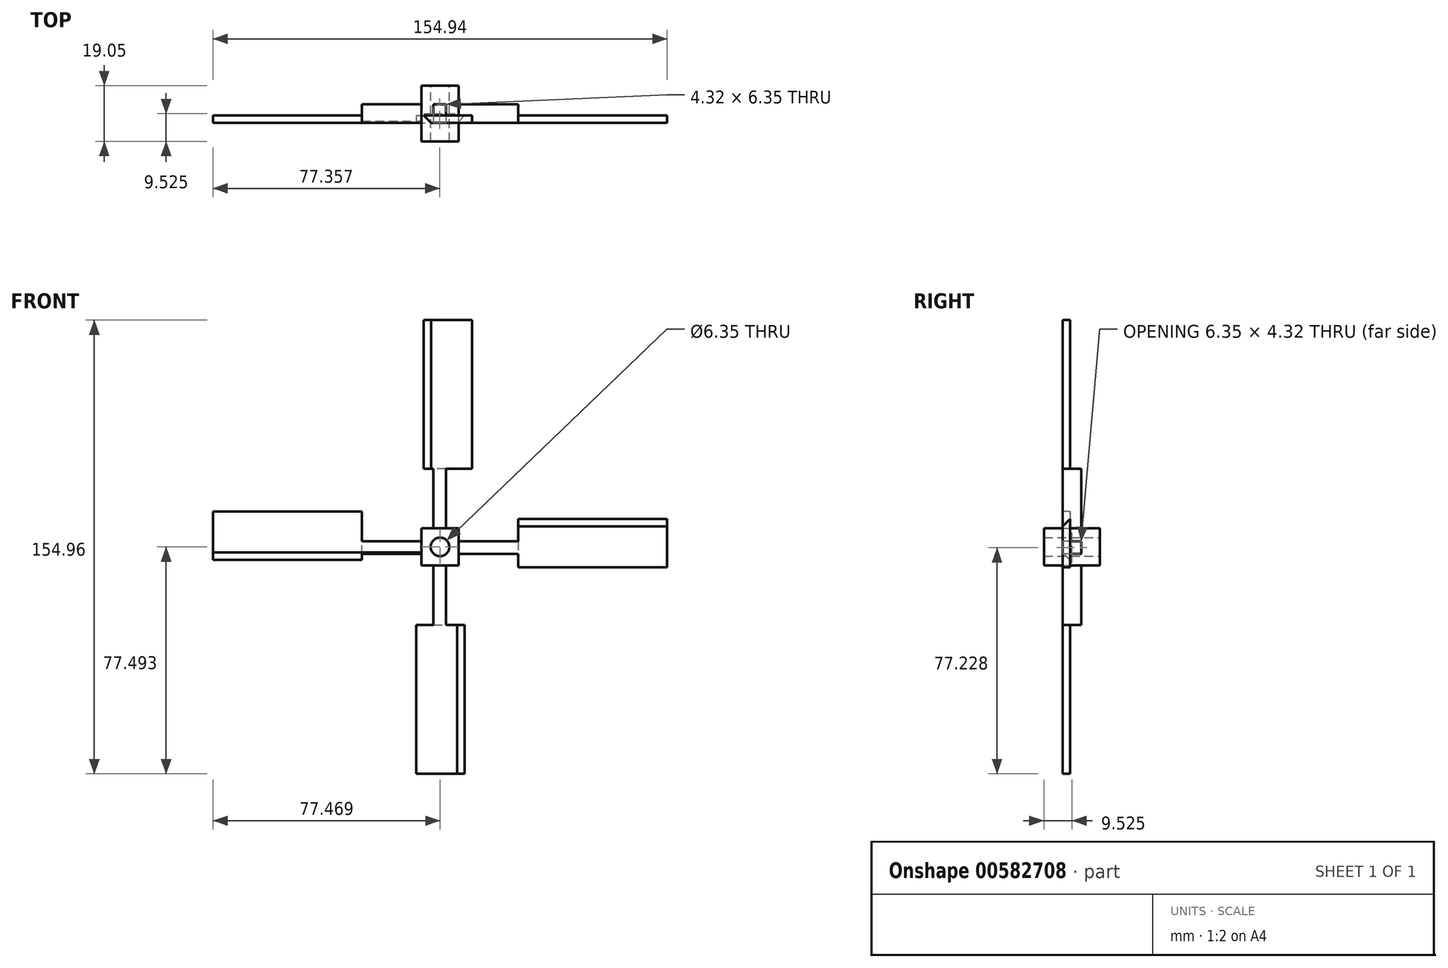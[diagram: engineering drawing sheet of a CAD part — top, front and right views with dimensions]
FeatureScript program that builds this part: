
annotation { "Feature Type Name" : "Feature", "Feature Type Description" : "" }
export const myFeature = defineFeature(function(context is Context, id is Id, definition is map)
    precondition{}
    {
        {
            var Q0;
            Q0=qCreatedBy(makeId("Front.planeOp"),FACE);
            var sketch = newSketch(context, id + "F0", { "sketchPlane" : qUnion([Q0])});
            skLineSegment(sketch, "E0", {"start": v(4.35, 3.5) * mm, "end": v(4.35, -9.2) * mm});
            skLineSegment(sketch, "E1", {"start": v(4.35, -9.2) * mm, "end": v(17.05, -9.2) * mm});
            skLineSegment(sketch, "E2", {"start": v(17.05, -9.2) * mm, "end": v(17.05, 3.5) * mm});
            skLineSegment(sketch, "E3", {"start": v(17.05, 3.5) * mm, "end": v(4.35, 3.5) * mm});
            skCircle(sketch, "E4", {"center": v(10.7, -2.85) * mm, "radius": 3.18 * mm});
            skPoint(sketch, "E4.centerSnap1", {"position": v(4.35, -2.85) * mm});
            skLineSegment(sketch, "E5", {"start": v(17.05, -0.95) * mm, "end": v(37.37, -0.95) * mm});
            skLineSegment(sketch, "E6", {"start": v(37.37, -0.95) * mm, "end": v(37.37, -5.27) * mm});
            skLineSegment(sketch, "E7", {"start": v(37.37, -5.27) * mm, "end": v(17.05, -5.27) * mm});
            skLineSegment(sketch, "E8", {"start": v(4.35, -5.27) * mm, "end": v(-15.97, -5.27) * mm});
            skLineSegment(sketch, "E9", {"start": v(-15.97, -5.27) * mm, "end": v(-15.97, -0.95) * mm});
            skLineSegment(sketch, "E10", {"start": v(-15.97, -0.95) * mm, "end": v(4.35, -0.95) * mm});
            skLineSegment(sketch, "E11", {"start": v(37.37, 9.26) * mm, "end": v(37.37, -0.95) * mm});
            skLineSegment(sketch, "E12", {"start": v(37.37, 9.26) * mm, "end": v(88.17, 9.26) * mm});
            skLineSegment(sketch, "E13", {"start": v(88.17, 9.26) * mm, "end": v(88.17, -9.79) * mm});
            skLineSegment(sketch, "E14", {"start": v(88.17, -9.79) * mm, "end": v(37.37, -9.79) * mm});
            skLineSegment(sketch, "E15", {"start": v(37.37, -9.79) * mm, "end": v(37.37, -5.27) * mm});
            skLineSegment(sketch, "E16", {"start": v(-15.97, -0.95) * mm, "end": v(-15.97, 9.26) * mm});
            skLineSegment(sketch, "E17", {"start": v(-15.97, 9.26) * mm, "end": v(-66.77, 9.26) * mm});
            skLineSegment(sketch, "E18", {"start": v(-66.77, 9.26) * mm, "end": v(-66.77, -9.79) * mm});
            skLineSegment(sketch, "E19", {"start": v(-66.77, -9.79) * mm, "end": v(-15.97, -9.79) * mm});
            skLineSegment(sketch, "E20", {"start": v(-15.97, -9.79) * mm, "end": v(-15.97, -5.27) * mm});
            skLineSegment(sketch, "E21", {"start": v(8.43, 3.5) * mm, "end": v(8.43, 23.82) * mm});
            skLineSegment(sketch, "E22", {"start": v(8.43, 23.82) * mm, "end": v(12.75, 23.82) * mm});
            skLineSegment(sketch, "E23", {"start": v(12.75, 23.82) * mm, "end": v(12.75, 3.5) * mm});
            skLineSegment(sketch, "E24", {"start": v(8.43, -9.2) * mm, "end": v(8.43, -29.52) * mm});
            skLineSegment(sketch, "E25", {"start": v(8.43, -29.52) * mm, "end": v(12.75, -29.52) * mm});
            skLineSegment(sketch, "E26", {"start": v(12.75, -29.52) * mm, "end": v(12.75, -9.2) * mm});
            skLineSegment(sketch, "E27", {"start": v(8.43, 23.82) * mm, "end": v(2.63, 23.82) * mm});
            skLineSegment(sketch, "E28", {"start": v(2.63, 23.82) * mm, "end": v(2.63, 74.62) * mm});
            skLineSegment(sketch, "E29", {"start": v(2.63, 74.62) * mm, "end": v(21.68, 74.62) * mm});
            skLineSegment(sketch, "E30", {"start": v(21.68, 74.62) * mm, "end": v(21.68, 23.82) * mm});
            skLineSegment(sketch, "E31", {"start": v(21.68, 23.82) * mm, "end": v(12.75, 23.82) * mm});
            skLineSegment(sketch, "E32", {"start": v(8.43, -29.52) * mm, "end": v(2.63, -29.52) * mm});
            skLineSegment(sketch, "E33", {"start": v(21.68, -29.52) * mm, "end": v(12.75, -29.52) * mm});
            skLineSegment(sketch, "E34", {"start": v(2.63, -29.52) * mm, "end": v(2.63, -80.34) * mm});
            skLineSegment(sketch, "E35", {"start": v(2.63, -80.34) * mm, "end": v(21.68, -80.34) * mm});
            skLineSegment(sketch, "E36", {"start": v(21.68, -80.34) * mm, "end": v(21.68, -29.52) * mm});
            skSolve(sketch);
        }
        {
            var Q0;
            Q0=makeQuery(id+"F0.imprint","IMPRINT",FACE,{"disambiguationData":[TD([[makeQuery(id+"F0.imprint","IMPRINT",EDGE,{"derivedFrom":sQuery(id+"F0.wireOp",EDGE,"E4")}),-1.0]])]});
            extrude(context, id + "F1", {"entities" : qUnion([Q0]), "depth" : 6.35 * mm, "offsetDistance" : 25.4 * mm, "hasSecondDirection" : true, "secondDirectionOppositeDirection" : true, "secondDirectionDepth" : 12.7 * mm});
        }
        {
            var Q0;
            {var subQ0=sQuery(id+"F0.wireOp",EDGE,"E5");Q0=makeQuery(id+"F0.imprint","IMPRINT",FACE,{"disambiguationData":[TD([[makeQuery(id+"F0.imprint","IMPRINT",EDGE,{"derivedFrom":subQ0}),-1.0]])]});}
            var Q1;
            {var subQ0=sQuery(id+"F0.wireOp",EDGE,"E8");Q1=makeQuery(id+"F0.imprint","IMPRINT",FACE,{"disambiguationData":[TD([[makeQuery(id+"F0.imprint","IMPRINT",EDGE,{"derivedFrom":subQ0}),-1.0]])]});}
            var Q2;
            {var subQ0=sQuery(id+"F0.wireOp",EDGE,"E21");Q2=makeQuery(id+"F0.imprint","IMPRINT",FACE,{"disambiguationData":[TD([[makeQuery(id+"F0.imprint","IMPRINT",EDGE,{"derivedFrom":subQ0}),-1.0]])]});}
            var Q3;
            {var subQ0=sQuery(id+"F0.wireOp",EDGE,"E24");Q3=makeQuery(id+"F0.imprint","IMPRINT",FACE,{"disambiguationData":[TD([[makeQuery(id+"F0.imprint","IMPRINT",EDGE,{"derivedFrom":subQ0}),1.0]])]});}
            extrude(context, id + "F2", {"entities" : qUnion([Q0, Q1, Q2, Q3]), "operationType" : NewBodyOperationType.ADD, "oppositeDirection" : true, "depth" : 6.35 * mm, "offsetDistance" : 25.4 * mm});
        }
        {
            var Q0;
            Q0=makeQuery(id+"F0.imprint","IMPRINT",FACE,{"disambiguationData":[TD([[makeQuery(id+"F0.imprint","IMPRINT",EDGE,{"derivedFrom":sQuery(id+"F0.wireOp",EDGE,"E9")}),1.0]])]});
            var Q1;
            Q1=makeQuery(id+"F0.imprint","IMPRINT",FACE,{"disambiguationData":[TD([[makeQuery(id+"F0.imprint","IMPRINT",EDGE,{"derivedFrom":sQuery(id+"F0.wireOp",EDGE,"E22")}),1.0]])]});
            var Q2;
            Q2=makeQuery(id+"F0.imprint","IMPRINT",FACE,{"disambiguationData":[TD([[makeQuery(id+"F0.imprint","IMPRINT",EDGE,{"derivedFrom":sQuery(id+"F0.wireOp",EDGE,"E6")}),1.0]])]});
            var Q3;
            Q3=makeQuery(id+"F0.imprint","IMPRINT",FACE,{"disambiguationData":[TD([[makeQuery(id+"F0.imprint","IMPRINT",EDGE,{"derivedFrom":sQuery(id+"F0.wireOp",EDGE,"E25")}),-1.0]])]});
            extrude(context, id + "F3", {"entities" : qUnion([Q0, Q1, Q2, Q3]), "operationType" : NewBodyOperationType.ADD, "oppositeDirection" : true, "depth" : 2.54 * mm, "offsetDistance" : 25.4 * mm});
        }
        {
            var Q0;
            Q0=makeQuery(id+"F3.opExtrude","CAP_EDGE",EDGE,{"disambiguationData":[OSD([sQuery(id+"F0.wireOp",EDGE,"E19")])],"isStart":true});
            var Q1;
            Q1=makeQuery(id+"F3.opExtrude","CAP_EDGE",EDGE,{"disambiguationData":[OSD([sQuery(id+"F0.wireOp",EDGE,"E36")])],"isStart":true});
            var Q2;
            Q2=makeQuery(id+"F3.opExtrude","CAP_EDGE",EDGE,{"disambiguationData":[OSD([sQuery(id+"F0.wireOp",EDGE,"E12")])],"isStart":true});
            var Q3;
            Q3=makeQuery(id+"F3.opExtrude","CAP_EDGE",EDGE,{"disambiguationData":[OSD([sQuery(id+"F0.wireOp",EDGE,"E28")])],"isStart":true});
            chamfer(context, id + "F4", {"entities" : qUnion([Q0, Q1, Q2, Q3]), "width" : 5.08 * mm, "tangentPropagation" : true});
        }
    });
